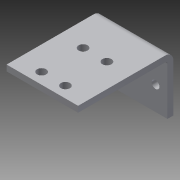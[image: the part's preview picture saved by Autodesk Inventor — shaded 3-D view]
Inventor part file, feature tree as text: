
AUTODESK INVENTOR PART (.ipt)
format: ipt  version: 2014 (Build 180170000, 170)  size: 129,024 bytes
history: native  units: in
note: dims shown in document units (in); Inventor stores cm internally (conversion verified against a paired STEP export)
features: sheet_metal_op x4, sketch x3, other x3
ambient origin geometry x8: Origin, YZ Plane, XZ Plane, XY Plane, X Axis, Y Axis, Z Axis, Center Point
bodies: Solid1 (feature_tree)
feature tree (10):
  sheet_metal_op  "Face1"
  sheet_metal_op  "Flange1"
  sketch  "Sketch1"  dims[d0=1.5in]
  other  "Plate1"
  sketch  "Sketch2"  dims[d1=1.0in]
  other  "Plate2"
  sheet_metal_op  "Bend1"
  sheet_metal_op  "Corner1"
  sketch  "Sketch3"  dims[d2=0.163in d3=0.5in d4=0.25in d5=0.7874in d7=1.0in d8=0.3937in d10=1.0in d12=0.125in d13=0.125in d14=0.0625in d15=0.25in d16=0.125in d17=2.0in d18=90.0deg d19=0.05in d20=0.5in d21=0.125in d22=0.125in d23=0.75in d24=1.31in d25=0.22in d26=0.125in d27=0.19in d28=0.375in d29=0.5in d30=0.125in d31=0.0in]
  other  "Cut1"
